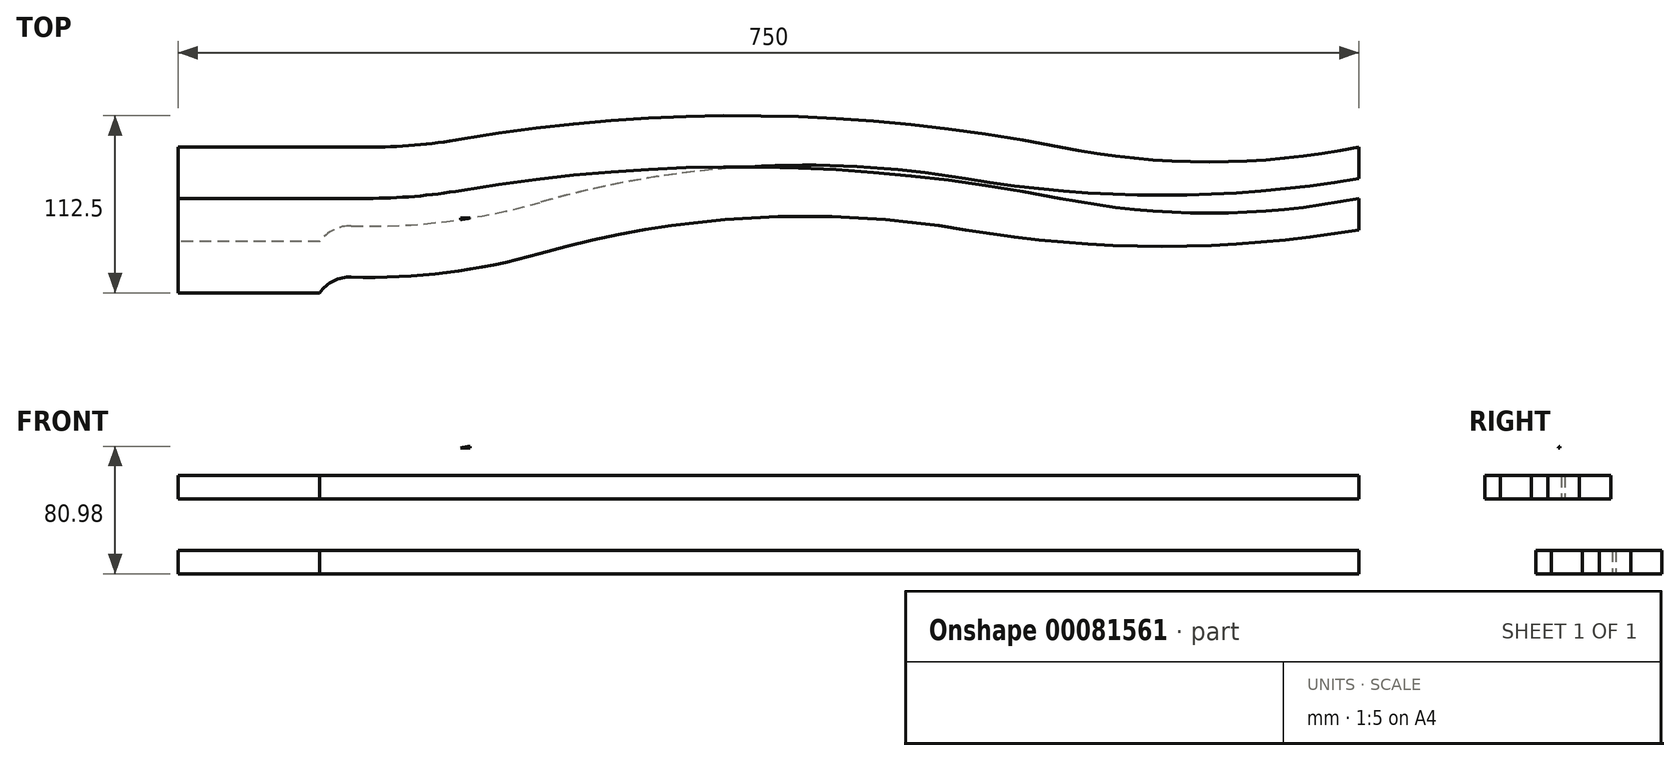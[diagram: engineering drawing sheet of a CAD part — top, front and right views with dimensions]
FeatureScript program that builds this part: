
annotation { "Feature Type Name" : "Feature", "Feature Type Description" : "" }
export const myFeature = defineFeature(function(context is Context, id is Id, definition is map)
    precondition{}
    {
        {
            var Q0;
            Q0=qCreatedBy(makeId("Front.planeOp"),FACE);
            var sketch = newSketch(context, id + "F0", { "sketchPlane" : qUnion([Q0])});
            skLineSegment(sketch, "E0.bottom", {"start": v(-375, 40) * mm, "end": v(375, 40) * mm, "construction": true});
            skLineSegment(sketch, "E0.top", {"start": v(-375, -40) * mm, "end": v(375, -40) * mm, "construction": true});
            skLineSegment(sketch, "E0.left", {"start": v(-375, 40) * mm, "end": v(-375, -40) * mm, "construction": true});
            skLineSegment(sketch, "E0.right", {"start": v(375, 40) * mm, "end": v(375, -40) * mm, "construction": true});
            skArc(sketch, "E1", {"start": v(-375, -40) * mm, "mid": v(-357.43, 2.43) * mm, "end": v(-315, 20) * mm, "construction": true});
            skLineSegment(sketch, "E2", {"start": v(-315, 20) * mm, "end": v(-255, 20) * mm});
            skArc(sketch, "E3", {"start": v(-255, 20) * mm, "mid": v(-224.9, 21.27) * mm, "end": v(-195, 25.08) * mm});
            skArc(sketch, "E4", {"start": v(-195, 25.08) * mm, "mid": v(-4.77, 39.9) * mm, "end": v(185, 20) * mm});
            skArc(sketch, "E5", {"start": v(185, 20) * mm, "mid": v(280, 10.68) * mm, "end": v(375, 20) * mm});
            skLineSegment(sketch, "E6", {"start": v(375, 20) * mm, "end": v(375, 0) * mm});
            skArc(sketch, "E7", {"start": v(375, 0) * mm, "mid": v(250, -10.5) * mm, "end": v(125, 0) * mm});
            skArc(sketch, "E8", {"start": v(125, 0) * mm, "mid": v(-10.84, 7.61) * mm, "end": v(-145, -15) * mm});
            skArc(sketch, "E9", {"start": v(-145, -15) * mm, "mid": v(-204.42, -27.13) * mm, "end": v(-265, -30) * mm});
            skArc(sketch, "E10", {"start": v(-265, -30) * mm, "mid": v(-276.26, -32.48) * mm, "end": v(-285, -40) * mm});
            skLineSegment(sketch, "E11", {"start": v(-371.48, -189.6) * mm, "end": v(-262.02, 0) * mm, "construction": true});
            skLineSegment(sketch, "E12", {"start": v(-285, -40) * mm, "end": v(-375, -40) * mm});
            skLineSegment(sketch, "E13", {"start": v(-315, 20) * mm, "end": v(-375, 20) * mm});
            skLineSegment(sketch, "E14", {"start": v(-375, 20) * mm, "end": v(-375, -40) * mm});
            skSolve(sketch);
        }
        {
            var Q0;
            Q0=qSketchRegion(id+"F0",true);
            extrude(context, id + "F1", {"entities" : qUnion([Q0]), "endBound" : BoundingType.SYMMETRIC, "depth" : 15 * mm});
        }
        {
            var Q0;
            Q0=qCreatedBy(makeId("Top.planeOp"),FACE);
            var sketch = newSketch(context, id + "F2", { "sketchPlane" : qUnion([Q0])});
            skLineSegment(sketch, "E15", {"start": v(0, 0) * mm, "end": v(-379.1, 0) * mm, "construction": true});
            skSolve(sketch);
        }
        {
            var Q0;
            Q0=makeQuery(id+"F1.opExtrude","SWEPT_BODY",BODY,{"disambiguationData":[OSD([sQuery(id+"F0.wireOp",EDGE,"E1"),sQuery(id+"F0.wireOp",EDGE,"E2"),sQuery(id+"F0.wireOp",EDGE,"E3"),sQuery(id+"F0.wireOp",EDGE,"E4"),sQuery(id+"F0.wireOp",EDGE,"E5"),sQuery(id+"F0.wireOp",EDGE,"E6"),sQuery(id+"F0.wireOp",EDGE,"E7"),sQuery(id+"F0.wireOp",EDGE,"E8"),sQuery(id+"F0.wireOp",EDGE,"E9"),sQuery(id+"F0.wireOp",EDGE,"E10"),sQuery(id+"F0.wireOp",EDGE,"E12")])]});
            var Q1;
            Q1=sQuery(id+"F2.wireOp",EDGE,"E15");
            transform(context, id + "F3", {"entities" : qUnion([Q0]), "transformType" : TransformType.ROTATION, "transformAxis" : qUnion([Q1]), "angle" : 90 * degree, "makeCopy" : true});
        }
        {
            var Q0;
            Q0=makeQuery(id+"F3.opPattern","COPY",BODY,{"derivedFrom":makeQuery(id+"F1.opExtrude","SWEPT_BODY",BODY,{"disambiguationData":[OSD([sQuery(id+"F0.wireOp",EDGE,"E1"),sQuery(id+"F0.wireOp",EDGE,"E2"),sQuery(id+"F0.wireOp",EDGE,"E3"),sQuery(id+"F0.wireOp",EDGE,"E4"),sQuery(id+"F0.wireOp",EDGE,"E5"),sQuery(id+"F0.wireOp",EDGE,"E6"),sQuery(id+"F0.wireOp",EDGE,"E7"),sQuery(id+"F0.wireOp",EDGE,"E8"),sQuery(id+"F0.wireOp",EDGE,"E9"),sQuery(id+"F0.wireOp",EDGE,"E10"),sQuery(id+"F0.wireOp",EDGE,"E12")])]}),"instanceName":"1"});
            transform(context, id + "F4", {"entities" : qUnion([Q0]), "transformType" : TransformType.TRANSLATION_3D, "dx" : 0 * mm, "dy" : 13.43 * mm, "dz" : 0 * mm, "makeCopy" : true});
        }
        {
            var Q0;
            Q0=makeQuery(id+"F4.opPattern","COPY",BODY,{"derivedFrom":makeQuery(id+"F3.opPattern","COPY",BODY,{"derivedFrom":makeQuery(id+"F1.opExtrude","SWEPT_BODY",BODY,{"disambiguationData":[OSD([sQuery(id+"F0.wireOp",EDGE,"E1"),sQuery(id+"F0.wireOp",EDGE,"E2"),sQuery(id+"F0.wireOp",EDGE,"E3"),sQuery(id+"F0.wireOp",EDGE,"E4"),sQuery(id+"F0.wireOp",EDGE,"E5"),sQuery(id+"F0.wireOp",EDGE,"E6"),sQuery(id+"F0.wireOp",EDGE,"E7"),sQuery(id+"F0.wireOp",EDGE,"E8"),sQuery(id+"F0.wireOp",EDGE,"E9"),sQuery(id+"F0.wireOp",EDGE,"E10"),sQuery(id+"F0.wireOp",EDGE,"E12")])]}),"instanceName":"1"}),"instanceName":"1"});
            transform(context, id + "F5", {"entities" : qUnion([Q0]), "transformType" : TransformType.TRANSLATION_3D, "dx" : 0 * mm, "dy" : 0 * mm, "dz" : -13.98 * mm, "makeCopy" : true});
        }
        {
            var Q0;
            Q0=makeQuery(id+"F4.opPattern","COPY",BODY,{"derivedFrom":makeQuery(id+"F3.opPattern","COPY",BODY,{"derivedFrom":makeQuery(id+"F1.opExtrude","SWEPT_BODY",BODY,{"disambiguationData":[OSD([sQuery(id+"F0.wireOp",EDGE,"E1"),sQuery(id+"F0.wireOp",EDGE,"E2"),sQuery(id+"F0.wireOp",EDGE,"E3"),sQuery(id+"F0.wireOp",EDGE,"E4"),sQuery(id+"F0.wireOp",EDGE,"E5"),sQuery(id+"F0.wireOp",EDGE,"E6"),sQuery(id+"F0.wireOp",EDGE,"E7"),sQuery(id+"F0.wireOp",EDGE,"E8"),sQuery(id+"F0.wireOp",EDGE,"E9"),sQuery(id+"F0.wireOp",EDGE,"E10"),sQuery(id+"F0.wireOp",EDGE,"E12")])]}),"instanceName":"1"}),"instanceName":"1"});
            var Q1;
            Q1=makeQuery(id+"F5.opPattern","COPY",BODY,{"derivedFrom":makeQuery(id+"F4.opPattern","COPY",BODY,{"derivedFrom":makeQuery(id+"F3.opPattern","COPY",BODY,{"derivedFrom":makeQuery(id+"F1.opExtrude","SWEPT_BODY",BODY,{"disambiguationData":[OSD([sQuery(id+"F0.wireOp",EDGE,"E1"),sQuery(id+"F0.wireOp",EDGE,"E2"),sQuery(id+"F0.wireOp",EDGE,"E3"),sQuery(id+"F0.wireOp",EDGE,"E4"),sQuery(id+"F0.wireOp",EDGE,"E5"),sQuery(id+"F0.wireOp",EDGE,"E6"),sQuery(id+"F0.wireOp",EDGE,"E7"),sQuery(id+"F0.wireOp",EDGE,"E8"),sQuery(id+"F0.wireOp",EDGE,"E9"),sQuery(id+"F0.wireOp",EDGE,"E10"),sQuery(id+"F0.wireOp",EDGE,"E12")])]}),"instanceName":"1"}),"instanceName":"1"}),"instanceName":"1"});
            deleteBodies(context, id + "F6", {"entities" : qUnion([Q0, Q1])});
        }
        {
            var Q0;
            Q0=makeQuery(id+"F1.opExtrude","SWEPT_BODY",BODY,{"disambiguationData":[OSD([sQuery(id+"F0.wireOp",EDGE,"E1"),sQuery(id+"F0.wireOp",EDGE,"E2"),sQuery(id+"F0.wireOp",EDGE,"E3"),sQuery(id+"F0.wireOp",EDGE,"E4"),sQuery(id+"F0.wireOp",EDGE,"E5"),sQuery(id+"F0.wireOp",EDGE,"E6"),sQuery(id+"F0.wireOp",EDGE,"E7"),sQuery(id+"F0.wireOp",EDGE,"E8"),sQuery(id+"F0.wireOp",EDGE,"E9"),sQuery(id+"F0.wireOp",EDGE,"E10"),sQuery(id+"F0.wireOp",EDGE,"E12")])]});
            var Q1;
            Q1=makeQuery(id+"F1.opExtrude","CAP_EDGE",EDGE,{"disambiguationData":[OSD([sQuery(id+"F0.wireOp",EDGE,"E12")])],"isStart":false});
            transform(context, id + "F7", {"entities" : qUnion([Q0]), "transformType" : TransformType.ROTATION, "transformAxis" : qUnion([Q1]), "angle" : 90 * degree, "makeCopy" : true});
        }
        {
            var Q0;
            Q0=makeQuery(id+"F7.opPattern","COPY",BODY,{"derivedFrom":makeQuery(id+"F1.opExtrude","SWEPT_BODY",BODY,{"disambiguationData":[OSD([sQuery(id+"F0.wireOp",EDGE,"E1"),sQuery(id+"F0.wireOp",EDGE,"E2"),sQuery(id+"F0.wireOp",EDGE,"E3"),sQuery(id+"F0.wireOp",EDGE,"E4"),sQuery(id+"F0.wireOp",EDGE,"E5"),sQuery(id+"F0.wireOp",EDGE,"E6"),sQuery(id+"F0.wireOp",EDGE,"E7"),sQuery(id+"F0.wireOp",EDGE,"E8"),sQuery(id+"F0.wireOp",EDGE,"E9"),sQuery(id+"F0.wireOp",EDGE,"E10"),sQuery(id+"F0.wireOp",EDGE,"E12")])]}),"instanceName":"1"});
            transform(context, id + "F8", {"entities" : qUnion([Q0]), "transformType" : TransformType.TRANSLATION_3D, "dx" : 0 * mm, "dy" : 0 * mm, "dz" : 80 * mm, "makeCopy" : true});
        }
        {
            var Q0;
            Q0=makeQuery(id+"F8.opPattern","COPY",BODY,{"derivedFrom":makeQuery(id+"F7.opPattern","COPY",BODY,{"derivedFrom":makeQuery(id+"F1.opExtrude","SWEPT_BODY",BODY,{"disambiguationData":[OSD([sQuery(id+"F0.wireOp",EDGE,"E1"),sQuery(id+"F0.wireOp",EDGE,"E2"),sQuery(id+"F0.wireOp",EDGE,"E3"),sQuery(id+"F0.wireOp",EDGE,"E4"),sQuery(id+"F0.wireOp",EDGE,"E5"),sQuery(id+"F0.wireOp",EDGE,"E6"),sQuery(id+"F0.wireOp",EDGE,"E7"),sQuery(id+"F0.wireOp",EDGE,"E8"),sQuery(id+"F0.wireOp",EDGE,"E9"),sQuery(id+"F0.wireOp",EDGE,"E10"),sQuery(id+"F0.wireOp",EDGE,"E12")])]}),"instanceName":"1"}),"instanceName":"1"});
            var Q1;
            Q1=makeQuery(id+"F1.opExtrude","SWEPT_BODY",BODY,{"disambiguationData":[OSD([sQuery(id+"F0.wireOp",EDGE,"E1"),sQuery(id+"F0.wireOp",EDGE,"E2"),sQuery(id+"F0.wireOp",EDGE,"E3"),sQuery(id+"F0.wireOp",EDGE,"E4"),sQuery(id+"F0.wireOp",EDGE,"E5"),sQuery(id+"F0.wireOp",EDGE,"E6"),sQuery(id+"F0.wireOp",EDGE,"E7"),sQuery(id+"F0.wireOp",EDGE,"E8"),sQuery(id+"F0.wireOp",EDGE,"E9"),sQuery(id+"F0.wireOp",EDGE,"E10"),sQuery(id+"F0.wireOp",EDGE,"E12")])]});
            booleanBodies(context, id + "F9", {"operationType" : BooleanOperationType.INTERSECTION, "tools" : qUnion([Q0, Q1])});
        }
        {
            var Q0;
            {var subQ0=makeQuery(id+"F1.opExtrude","SWEPT_BODY",BODY,{"disambiguationData":[OSD([sQuery(id+"F0.wireOp",EDGE,"E1"),sQuery(id+"F0.wireOp",EDGE,"E2"),sQuery(id+"F0.wireOp",EDGE,"E3"),sQuery(id+"F0.wireOp",EDGE,"E4"),sQuery(id+"F0.wireOp",EDGE,"E5"),sQuery(id+"F0.wireOp",EDGE,"E6"),sQuery(id+"F0.wireOp",EDGE,"E7"),sQuery(id+"F0.wireOp",EDGE,"E8"),sQuery(id+"F0.wireOp",EDGE,"E9"),sQuery(id+"F0.wireOp",EDGE,"E10"),sQuery(id+"F0.wireOp",EDGE,"E12")])]});Q0=makeQuery(id+"F9.opBoolean","INTERSECT",BODY,{"derivedFrom":[subQ0,makeQuery(id+"F8.opPattern","COPY",BODY,{"derivedFrom":makeQuery(id+"F7.opPattern","COPY",BODY,{"derivedFrom":subQ0,"instanceName":"1"}),"instanceName":"1"})]});}
            transform(context, id + "F10", {"entities" : qUnion([Q0]), "transformType" : TransformType.TRANSLATION_3D, "dx" : 0 * mm, "dy" : 0 * mm, "dz" : -1000 * mm, "makeCopy" : true});
        }
        {
            var Q0;
            {var subQ0=makeQuery(id+"F1.opExtrude","SWEPT_BODY",BODY,{"disambiguationData":[OSD([sQuery(id+"F0.wireOp",EDGE,"E1"),sQuery(id+"F0.wireOp",EDGE,"E2"),sQuery(id+"F0.wireOp",EDGE,"E3"),sQuery(id+"F0.wireOp",EDGE,"E4"),sQuery(id+"F0.wireOp",EDGE,"E5"),sQuery(id+"F0.wireOp",EDGE,"E6"),sQuery(id+"F0.wireOp",EDGE,"E7"),sQuery(id+"F0.wireOp",EDGE,"E8"),sQuery(id+"F0.wireOp",EDGE,"E9"),sQuery(id+"F0.wireOp",EDGE,"E10"),sQuery(id+"F0.wireOp",EDGE,"E12")])]});Q0=makeQuery(id+"F10.opPattern","COPY",BODY,{"derivedFrom":makeQuery(id+"F9.opBoolean","INTERSECT",BODY,{"derivedFrom":[subQ0,makeQuery(id+"F8.opPattern","COPY",BODY,{"derivedFrom":makeQuery(id+"F7.opPattern","COPY",BODY,{"derivedFrom":subQ0,"instanceName":"1"}),"instanceName":"1"})]}),"instanceName":"1"});}
            deleteBodies(context, id + "F11", {"entities" : qUnion([Q0])});
        }
    });
